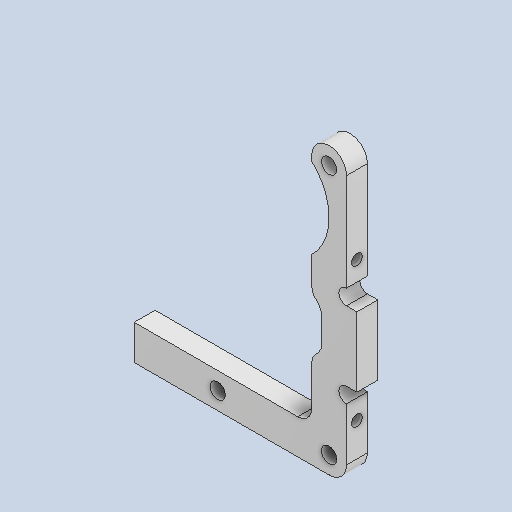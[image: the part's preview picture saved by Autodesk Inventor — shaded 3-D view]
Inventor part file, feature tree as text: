
AUTODESK INVENTOR PART (.ipt)
format: ipt  version: 2025.1 (Build 291241000, 241)  size: 252,416 bytes
history: native  units: mm
features: reference x11, other x6, sketch x3, fillet x2, hole x2, extrude x1
ambient origin geometry x8: Origin, YZ Plane, XZ Plane, XY Plane, X Axis, Y Axis, Z Axis, Center Point
bodies: Body1 (feature_tree)
feature tree (25):
  other  "ソリッド1"
  extrude  "押し出し1"  Depth=2.2mm
  fillet  "フィレット1"  Radius=2.2mm
  hole  "穴1"  [1 undecoded]
  hole  "穴2"  [1 undecoded]
  fillet  "フィレット2"  Radius=2.2mm
  sketch  "スケッチ1"
  reference  "参照1"
  reference  "参照2"
  reference  "参照3"
  reference  "参照4"
  reference  "参照5"
  reference  "参照6"
  reference  "参照7"
  reference  "参照8"
  reference  "参照9"
  sketch  "スケッチ2"
  reference  "参照10"
  reference  "参照11"
  sketch  "スケッチ3"
  other  "<userpath>\Documents\Inventor\Vixen\doutai.iam"
  other  "doutai.iam"
  other  "KRS2500_scale:8"
  other  "KSHI:1"
  other  "KRS2500_scale:1"
note: 2 required parameter values undecoded (feature->parameter linkage not recoverable at this tier; creation-order binding heuristic only, values carry confidence <= 0.55)
